# Revit family: ASSA_ABLOY_HPD_HS9030GAT
name_source: partatom
category: Doors
units: mm (PartAtom-declared; Revit-internal decimal feet)

## family parameters
Always vertical = Yes
Cut with Voids When Loaded = No
Host = Wall
Room Calculation Point = No
Shared = No

## types (1)
- Type 1
    Air permeability, EN 12426 = Class 4 (3 m³/m²/h at 50 Pa) Overpressure, Class 3 (6 m³/m²/h at 50 Pa) Underpressure
    Analytic Construction = <None>
    Area of use = Inside
    ColumnCover = Yes
    Description = High Performance Door
    DrumCover = Yes
    DrumCoverMotorOnTheLeft = No
    Manufacturer = ASSA ABLOY
    Model = HS9030GAT
    MotorOnTheRight = Yes
    Operating speed = Opening: up to 2,7 m/s, Closing: 0,5 m/s
    PVCWindows = Yes
    Performance Test, EN 12604 = 1.000.000 cycles
    Temperature working range = 5 °C to +40 °C
    Thermal transmittance, EN 12428 = 6,02 W/(m²K)
    URL = https://www.assaabloyentrance.com
    WDDForBottomBag = No
    WDDForBottomBagLeft = No
    WDDForBottomBagRight = No
    Water penetration, EN 12425 = Class 3 (>50 Pa (N/m²))
    Wind load resistance, EN 12424 = Class 1 (300 Pa (N/m²)) maximum wind load while closing 50 Pa (N/m²)
    WindowMaterial = Transparent

## geometry (parser evidence)
native form markers: Sweep x17
no freeform markers — native parametric forms only
